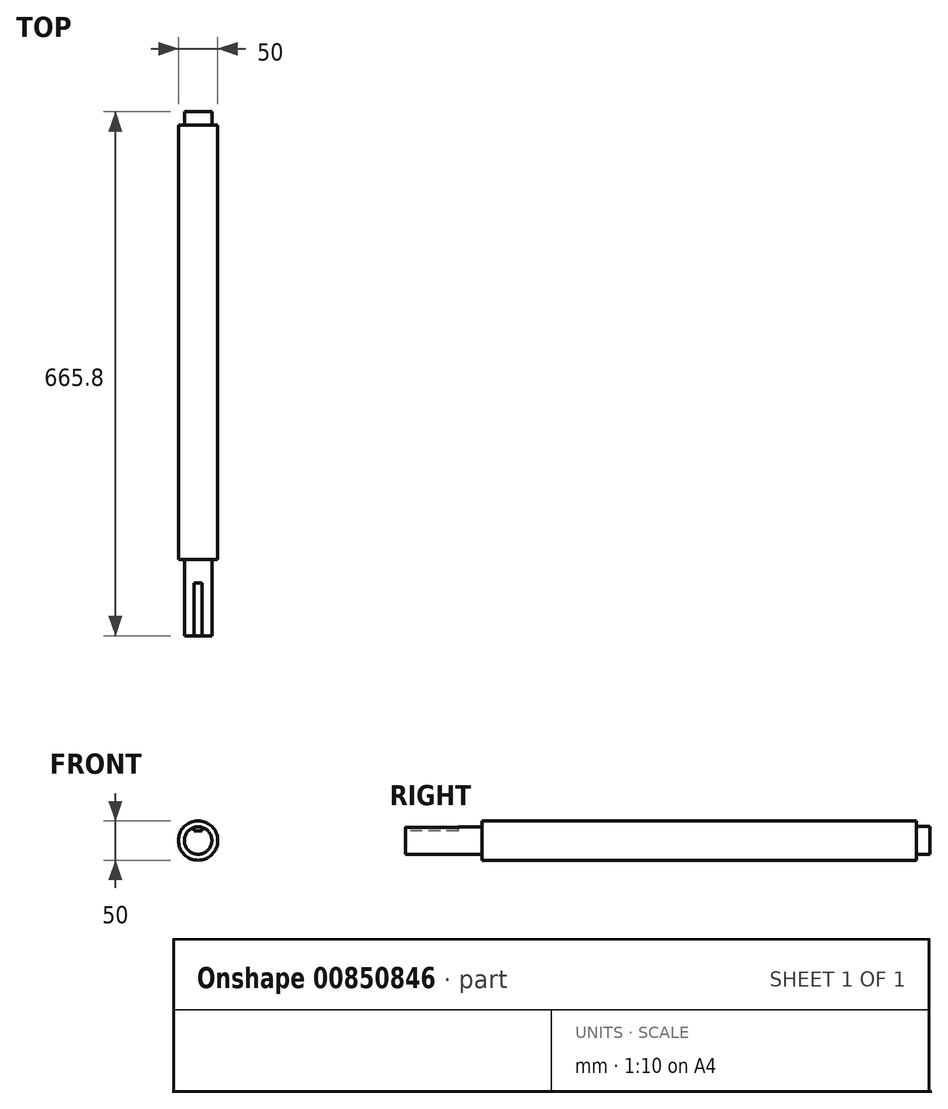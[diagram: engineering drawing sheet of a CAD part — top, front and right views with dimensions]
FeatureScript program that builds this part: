
annotation { "Feature Type Name" : "Feature", "Feature Type Description" : "" }
export const myFeature = defineFeature(function(context is Context, id is Id, definition is map)
    precondition{}
    {
        {
            var Q0;
            Q0=qCreatedBy(makeId("Front.planeOp"),FACE);
            var sketch = newSketch(context, id + "F0", { "sketchPlane" : qUnion([Q0])});
            skCircle(sketch, "E0", {"center": v(-99.98, 13.99) * mm, "radius": 25 * mm});
            skSolve(sketch);
        }
        {
            var Q0;
            Q0=makeQuery(id+"F0.imprint","IMPRINT",FACE,{"disambiguationData":[TD([[makeQuery(id+"F0.imprint","IMPRINT",EDGE,{"derivedFrom":sQuery(id+"F0.wireOp",EDGE,"E0")}),1.0]])]});
            extrude(context, id + "F1", {"entities" : qUnion([Q0]), "depth" : 665.8 * mm, "offsetDistance" : 25.4 * mm});
        }
        {
            var Q0;
            Q0=makeQuery(id+"F1.opExtrude","CAP_FACE",FACE,{"disambiguationData":[OSD([sQuery(id+"F0.wireOp",EDGE,"E0")])],"isStart":false});
            var sketch = newSketch(context, id + "F2", { "sketchPlane" : qUnion([Q0])});
            skCircle(sketch, "E1", {"center": v(-99.98, 13.99) * mm, "radius": 17.5 * mm});
            skSolve(sketch);
        }
        {
            var Q0;
            Q0=makeQuery(id+"F2.imprint","IMPRINT",FACE,{"disambiguationData":[TD([[makeQuery(id+"F2.imprint","IMPRINT",EDGE,{"derivedFrom":sQuery(id+"F2.wireOp",EDGE,"E1")}),-1.0]])]});
            extrude(context, id + "F3", {"entities" : qUnion([Q0]), "operationType" : NewBodyOperationType.REMOVE, "oppositeDirection" : true, "depth" : 97 * mm, "offsetDistance" : 25.4 * mm});
        }
        {
            var Q0;
            Q0=makeQuery(id+"F0.imprint","IMPRINT",FACE,{"disambiguationData":[TD([[makeQuery(id+"F0.imprint","IMPRINT",EDGE,{"derivedFrom":sQuery(id+"F0.wireOp",EDGE,"E0")}),1.0]])]});
            var sketch = newSketch(context, id + "F4", { "sketchPlane" : qUnion([Q0])});
            skCircle(sketch, "E2", {"center": v(-99.9, 14.12) * mm, "radius": 17.5 * mm});
            skSolve(sketch);
        }
        {
            var Q0;
            Q0=makeQuery(id+"F4.imprint","IMPRINT",FACE,{"disambiguationData":[TD([[makeQuery(id+"F4.imprint","IMPRINT",EDGE,{"derivedFrom":sQuery(id+"F4.wireOp",EDGE,"E2")}),-1.0]])]});
            extrude(context, id + "F5", {"entities" : qUnion([Q0]), "operationType" : NewBodyOperationType.REMOVE, "depth" : 17 * mm, "offsetDistance" : 25.4 * mm});
        }
        {
            var Q0;
            Q0=makeQuery(id+"F2.imprint","IMPRINT",FACE,{"disambiguationData":[TD([[makeQuery(id+"F2.imprint","IMPRINT",EDGE,{"derivedFrom":sQuery(id+"F2.wireOp",EDGE,"E1")}),1.0]])]});
            var sketch = newSketch(context, id + "F6", { "sketchPlane" : qUnion([Q0])});
            skLineSegment(sketch, "E3", {"start": v(-104.96, 26.49) * mm, "end": v(-104.96, 30.76) * mm});
            skLineSegment(sketch, "E4", {"start": v(-94.96, 26.49) * mm, "end": v(-94.96, 30.76) * mm});
            skLineSegment(sketch, "E5", {"start": v(-104.96, 26.49) * mm, "end": v(-94.96, 26.49) * mm});
            skLineSegment(sketch, "E6", {"start": v(-104.96, 30.76) * mm, "end": v(-104.96, 30.76) * mm});
            skArc(sketch, "E7", {"start": v(-94.96, 30.76) * mm, "mid": v(-99.96, 31.62) * mm, "end": v(-104.96, 30.76) * mm});
            skSolve(sketch);
        }
        {
            var Q0;
            {var subQ5=sQuery(id+"F6.wireOp",EDGE,"E3");Q0=makeQuery(id+"F6.imprint","IMPRINT",FACE,{"disambiguationData":[TD([[makeQuery(id+"F6.imprint","IMPRINT",EDGE,{"derivedFrom":subQ5}),-1.0]])]});}
            extrude(context, id + "F7", {"entities" : qUnion([Q0]), "operationType" : NewBodyOperationType.REMOVE, "oppositeDirection" : true, "depth" : 67 * mm, "offsetDistance" : 25.4 * mm});
        }
    });
